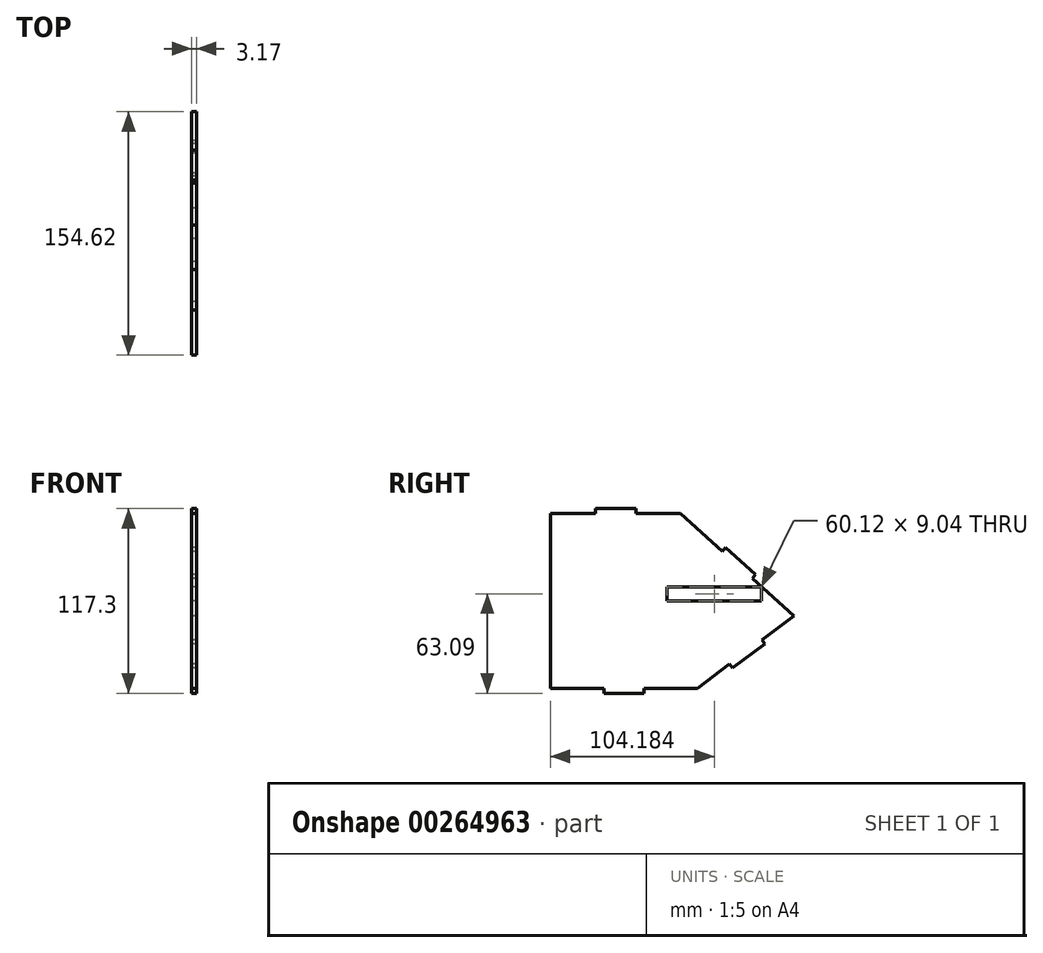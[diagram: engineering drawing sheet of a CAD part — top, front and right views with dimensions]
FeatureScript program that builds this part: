
annotation { "Feature Type Name" : "Feature", "Feature Type Description" : "" }
export const myFeature = defineFeature(function(context is Context, id is Id, definition is map)
    precondition{}
    {
        {
            var Q0;
            Q0=qCreatedBy(makeId("Right.planeOp"),FACE);
            var sketch = newSketch(context, id + "F0", { "sketchPlane" : qUnion([Q0])});
            skLineSegment(sketch, "E0", {"start": v(33.96, 45.94) * mm, "end": v(5.6, 45.94) * mm});
            skPoint(sketch, "E1.MirrorCS.end.orphan", {"position": v(-48.2, -63.5) * mm});
            skLineSegment(sketch, "E2", {"start": v(-48.65, 45.94) * mm, "end": v(-48.65, -65.02) * mm});
            skPoint(sketch, "E3.MirrorCS.start.orphan", {"position": v(-48.2, -63.34) * mm});
            skLineSegment(sketch, "E4", {"start": v(-48.65, -65.02) * mm, "end": v(-20.05, -65.02) * mm});
            skLineSegment(sketch, "E5", {"start": v(44.77, -65.02) * mm, "end": v(65.23, -49.6) * mm});
            skLineSegment(sketch, "E6", {"start": v(105.97, -18.9) * mm, "end": v(79.59, 4.85) * mm});
            skPoint(sketch, "E7.end.orphan", {"position": v(33.96, 48.11) * mm});
            skPoint(sketch, "E8", {"position": v(24.2, -9.62) * mm});
            skPoint(sketch, "E9", {"position": v(85.6, -0.58) * mm});
            skPoint(sketch, "E10.end.orphan", {"position": v(85.6, -9.62) * mm});
            skLineSegment(sketch, "E11.bottom", {"start": v(25.47, -9.62) * mm, "end": v(85.6, -9.62) * mm});
            skLineSegment(sketch, "E11.top", {"start": v(25.47, -0.58) * mm, "end": v(85.6, -0.58) * mm});
            skLineSegment(sketch, "E11.right", {"start": v(85.6, -9.62) * mm, "end": v(85.6, -0.58) * mm});
            skLineSegment(sketch, "E12.top", {"start": v(-7.35, 49.11) * mm, "end": v(-19.25, 49.11) * mm});
            skLineSegment(sketch, "E13.MirrorCS", {"start": v(-7.1, 49.11) * mm, "end": v(4.81, 49.11) * mm});
            skPoint(sketch, "E14.end.orphan", {"position": v(-20.05, 45.94) * mm});
            skPoint(sketch, "E12.left.start.orphan", {"position": v(-7.35, 45.94) * mm});
            skLineSegment(sketch, "E15.trimOffspring", {"start": v(-20.05, 45.94) * mm, "end": v(-48.65, 45.94) * mm});
            skLineSegment(sketch, "E16", {"start": v(-13.85, -68.2) * mm, "end": v(9.96, -68.2) * mm});
            skLineSegment(sketch, "E17.trimOffspring", {"start": v(11.01, -65.02) * mm, "end": v(44.77, -65.02) * mm});
            skLineSegment(sketch, "E18", {"start": v(72.09, 15.88) * mm, "end": v(63.24, 23.85) * mm});
            skLineSegment(sketch, "E19.MirrorCS", {"start": v(72.09, 15.88) * mm, "end": v(80.94, 7.91) * mm});
            skPoint(sketch, "E20.orphan", {"position": v(69.96, 13.52) * mm});
            skLineSegment(sketch, "E21.trimOffspring", {"start": v(60.52, 22.02) * mm, "end": v(33.96, 45.94) * mm});
            skLineSegment(sketch, "E22", {"start": v(77.28, -44.5) * mm, "end": v(86.79, -37.33) * mm});
            skLineSegment(sketch, "E23.MirrorCS", {"start": v(77.28, -44.5) * mm, "end": v(67.77, -51.66) * mm});
            skPoint(sketch, "E24.start.orphan", {"position": v(75.37, -41.96) * mm});
            skLineSegment(sketch, "E25.trimOffspring", {"start": v(85.71, -34.16) * mm, "end": v(105.97, -18.9) * mm});
            skLineSegment(sketch, "E26", {"start": v(-48.65, -65.02) * mm, "end": v(-14.64, -65.02) * mm});
            skPoint(sketch, "E27.end.orphan", {"position": v(-1.94, -68.2) * mm});
            skPoint(sketch, "E28.orphan", {"position": v(5.35, -65.02) * mm});
            skPoint(sketch, "E29.orphan", {"position": v(10.76, -65.02) * mm});
            skLineSegment(sketch, "E30", {"start": v(-7.35, 49.11) * mm, "end": v(-7.1, 49.11) * mm});
            skPoint(sketch, "E31.orphan", {"position": v(-20.05, 49.11) * mm});
            skPoint(sketch, "E32.orphan", {"position": v(5.35, 49.11) * mm});
            skLineSegment(sketch, "E33", {"start": v(65.23, -49.6) * mm, "end": v(65.86, -49.12) * mm});
            skLineSegment(sketch, "E34", {"start": v(77.28, -44.5) * mm, "end": v(76.36, -43.28) * mm});
            skPoint(sketch, "E35.end.orphan", {"position": v(-13.77, -68.2) * mm});
            skPoint(sketch, "E35.start.orphan", {"position": v(-13.77, -64.94) * mm});
            skPoint(sketch, "E36.MirrorCS.end.orphan", {"position": v(9.89, -68.2) * mm});
            skPoint(sketch, "E36.MirrorCS.start.orphan", {"position": v(9.89, -64.94) * mm});
            skPoint(sketch, "E37.orphan", {"position": v(-14.64, -68.2) * mm});
            skLineSegment(sketch, "E38", {"start": v(10.76, -65.02) * mm, "end": v(11.01, -65.02) * mm});
            skPoint(sketch, "E39.start.orphan", {"position": v(10.76, -68.2) * mm});
            skLineSegment(sketch, "E40", {"start": v(-20.05, 49.11) * mm, "end": v(-20.05, 45.94) * mm});
            skLineSegment(sketch, "E41", {"start": v(5.6, 45.94) * mm, "end": v(5.6, 49.11) * mm});
            skLineSegment(sketch, "E42", {"start": v(5.6, 49.11) * mm, "end": v(4.81, 49.11) * mm});
            skLineSegment(sketch, "E43", {"start": v(-19.25, 49.11) * mm, "end": v(-20.05, 49.11) * mm});
            skLineSegment(sketch, "E44", {"start": v(79.59, 4.85) * mm, "end": v(82.27, 7.83) * mm});
            skLineSegment(sketch, "E45", {"start": v(80.94, 7.91) * mm, "end": v(81.71, 7.21) * mm});
            skLineSegment(sketch, "E46", {"start": v(60.52, 22.02) * mm, "end": v(62.65, 24.38) * mm});
            skLineSegment(sketch, "E47", {"start": v(63.24, 23.85) * mm, "end": v(62.65, 24.38) * mm});
            skLineSegment(sketch, "E48", {"start": v(65.23, -49.6) * mm, "end": v(67.14, -52.14) * mm});
            skLineSegment(sketch, "E49", {"start": v(67.77, -51.66) * mm, "end": v(67.14, -52.14) * mm});
            skLineSegment(sketch, "E50", {"start": v(85.71, -34.16) * mm, "end": v(87.62, -36.7) * mm});
            skLineSegment(sketch, "E51", {"start": v(86.79, -37.33) * mm, "end": v(87.62, -36.7) * mm});
            skPoint(sketch, "E52.end.orphan", {"position": v(84.88, -34.8) * mm});
            skLineSegment(sketch, "E53", {"start": v(-13.85, -68.2) * mm, "end": v(-14.64, -68.2) * mm});
            skLineSegment(sketch, "E54", {"start": v(-14.64, -65.02) * mm, "end": v(-14.64, -68.2) * mm});
            skLineSegment(sketch, "E55", {"start": v(10.76, -65.02) * mm, "end": v(10.76, -68.2) * mm});
            skLineSegment(sketch, "E56", {"start": v(9.96, -68.2) * mm, "end": v(10.76, -68.2) * mm});
            skPoint(sketch, "E57", {"position": v(16.18, -0.58) * mm});
            skLineSegment(sketch, "E58", {"start": v(16.18, -9.62) * mm, "end": v(16.18, -0.58) * mm});
            skLineSegment(sketch, "E59", {"start": v(25.47, -9.62) * mm, "end": v(25.47, -0.58) * mm});
            skSolve(sketch);
        }
        {
            var Q0;
            Q0=makeQuery(id+"F0.imprint","IMPRINT",FACE,{"disambiguationData":[TD([[makeQuery(id+"F0.imprint","IMPRINT",EDGE,{"derivedFrom":sQuery(id+"F0.wireOp",EDGE,"E0")}),1.0]])]});
            extrude(context, id + "F1", {"entities" : qUnion([Q0]), "depth" : 3.17 * mm, "offsetDistance" : 25.4 * mm});
        }
    });
